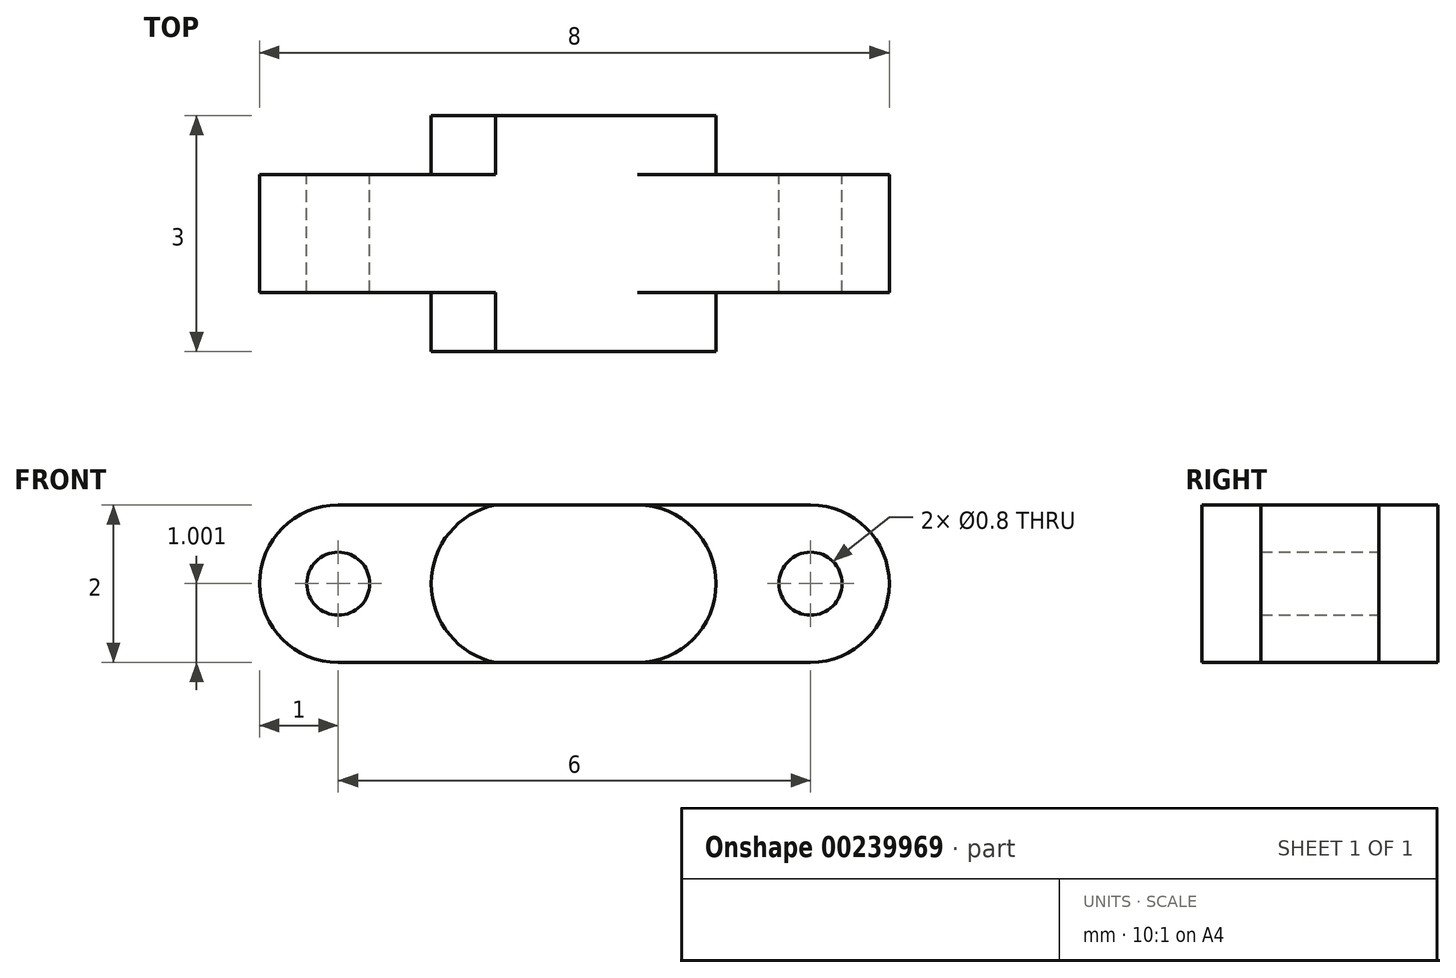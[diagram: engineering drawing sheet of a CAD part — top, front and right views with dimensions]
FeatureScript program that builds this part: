
annotation { "Feature Type Name" : "Feature", "Feature Type Description" : "" }
export const myFeature = defineFeature(function(context is Context, id is Id, definition is map)
    precondition{}
    {
        {
            var Q0;
            Q0=qCreatedBy(makeId("Front.planeOp"),FACE);
            var sketch = newSketch(context, id + "F0", { "sketchPlane" : qUnion([Q0])});
            skLineSegment(sketch, "E0.bottom", {"start": v(-1, -0.25) * mm, "end": v(-6, -0.25) * mm});
            skLineSegment(sketch, "E0.top", {"start": v(-1, -2.25) * mm, "end": v(-6, -2.25) * mm});
            skArc(sketch, "E1", {"start": v(0, -2.25) * mm, "mid": v(1, -1.25) * mm, "end": v(0, -0.25) * mm});
            skLineSegment(sketch, "E2", {"start": v(-1, -0.25) * mm, "end": v(0, -0.25) * mm});
            skLineSegment(sketch, "E3", {"start": v(-1, -2.25) * mm, "end": v(0, -2.25) * mm});
            skArc(sketch, "E4", {"start": v(-4, -0.25) * mm, "mid": v(-4.82, -1.25) * mm, "end": v(-4, -2.25) * mm});
            skPoint(sketch, "E5", {"position": v(-6, -1.25) * mm});
            skCircle(sketch, "E6", {"center": v(-6, -1.25) * mm, "radius": 0.4 * mm});
            skCircle(sketch, "E7", {"center": v(0, -1.25) * mm, "radius": 0.4 * mm});
            skArc(sketch, "E8", {"start": v(-2.2, -2.25) * mm, "mid": v(-1.2, -1.25) * mm, "end": v(-2.2, -0.25) * mm});
            skLineSegment(sketch, "E9", {"start": v(-6, -0.25) * mm, "end": v(-6, -0.25) * mm});
            skArc(sketch, "E10", {"start": v(-6, -0.25) * mm, "mid": v(-7, -1.25) * mm, "end": v(-6, -2.25) * mm});
            skLineSegment(sketch, "E11", {"start": v(-7, -1.25) * mm, "end": v(1, -1.25) * mm, "construction": true});
            skSolve(sketch);
        }
        {
            var Q0;
            {var subQ5=sQuery(id+"F0.wireOp",EDGE,"E4");Q0=makeQuery(id+"F0.imprint","IMPRINT",FACE,{"disambiguationData":[TD([[makeQuery(id+"F0.imprint","IMPRINT",EDGE,{"derivedFrom":subQ5}),1.0]])]});}
            var Q1;
            Q1=makeQuery(id+"F0.imprint","IMPRINT",FACE,{"disambiguationData":[TD([[makeQuery(id+"F0.imprint","IMPRINT",EDGE,{"derivedFrom":sQuery(id+"F0.wireOp",EDGE,"E1")}),1.0]])]});
            var Q2;
            {var subQ0=sQuery(id+"F0.wireOp",EDGE,"bQbziyav-jX1J-XLfE-gFu1-S9SHtQTFnJFi");var subQ1=sQuery(id+"F0.wireOp",EDGE,"Mre1yFln-Q6Go-vBB8-nmWn-4SXoC3vIunpy");var subQ2=makeQuery(id+"F0.imprint","INTERSECT",VERTEX,{"derivedFrom":[subQ1,subQ0]});Q2=makeQuery(id+"F0.imprint","IMPRINT",FACE,{"disambiguationData":[TD([[makeQuery(id+"F0.imprint","IMPRINT",EDGE,{"disambiguationData":[TD([[subQ2,1.0]])],"derivedFrom":subQ1}),1.0]])]});}
            var Q3;
            {var subQ1=sQuery(id+"F0.wireOp",EDGE,"E0.bottom");var subQ3=sQuery(id+"F0.wireOp",EDGE,"Mre1yFln-Q6Go-vBB8-nmWn-4SXoC3vIunpy");var subQ4=makeQuery(id+"F0.imprint","INTERSECT",VERTEX,{"derivedFrom":[subQ1,subQ3]});Q3=makeQuery(id+"F0.imprint","IMPRINT",FACE,{"disambiguationData":[TD([[makeQuery(id+"F0.imprint","IMPRINT",EDGE,{"disambiguationData":[TD([[subQ4,-1.0]])],"derivedFrom":subQ3}),1.0]])]});}
            var Q4;
            {var subQ1=sQuery(id+"F0.wireOp",EDGE,"E0.top");var subQ3=sQuery(id+"F0.wireOp",EDGE,"bQbziyav-jX1J-XLfE-gFu1-S9SHtQTFnJFi");var subQ4=makeQuery(id+"F0.imprint","INTERSECT",VERTEX,{"derivedFrom":[subQ1,subQ3]});Q4=makeQuery(id+"F0.imprint","IMPRINT",FACE,{"disambiguationData":[TD([[makeQuery(id+"F0.imprint","IMPRINT",EDGE,{"disambiguationData":[TD([[subQ4,1.0]])],"derivedFrom":subQ3}),1.0]])]});}
            var Q5;
            {var subQ0=sQuery(id+"F0.wireOp",EDGE,"E4");Q5=makeQuery(id+"F0.imprint","IMPRINT",FACE,{"disambiguationData":[TD([[makeQuery(id+"F0.imprint","IMPRINT",EDGE,{"derivedFrom":subQ0}),-1.0]])]});}
            var Q6;
            {var subQ1=sQuery(id+"F0.wireOp",EDGE,"E0.bottom");var subQ3=sQuery(id+"F0.wireOp",EDGE,"E8");var subQ4=makeQuery(id+"F0.imprint","INTERSECT",VERTEX,{"derivedFrom":[subQ1,subQ3]});Q6=makeQuery(id+"F0.imprint","IMPRINT",FACE,{"disambiguationData":[TD([[makeQuery(id+"F0.imprint","IMPRINT",EDGE,{"disambiguationData":[TD([[subQ4,1.0]])],"derivedFrom":subQ3}),-1.0]])]});}
            var Q7;
            {var subQ1=sQuery(id+"F0.wireOp",EDGE,"E0.top");var subQ3=sQuery(id+"F0.wireOp",EDGE,"E8");var subQ4=makeQuery(id+"F0.imprint","INTERSECT",VERTEX,{"derivedFrom":[subQ1,subQ3]});Q7=makeQuery(id+"F0.imprint","IMPRINT",FACE,{"disambiguationData":[TD([[makeQuery(id+"F0.imprint","IMPRINT",EDGE,{"disambiguationData":[TD([[subQ4,-1.0]])],"derivedFrom":subQ3}),-1.0]])]});}
            extrude(context, id + "F1", {"entities" : qUnion([Q0, Q1, Q2, Q3, Q4, Q5, Q6, Q7]), "depth" : 1.5 * mm});
        }
        {
            var Q0;
            {var subQ0=sQuery(id+"F0.wireOp",EDGE,"E4");Q0=makeQuery(id+"F0.imprint","IMPRINT",FACE,{"disambiguationData":[TD([[makeQuery(id+"F0.imprint","IMPRINT",EDGE,{"derivedFrom":subQ0}),1.0]])]});}
            var Q1;
            {var subQ0=sQuery(id+"F0.wireOp",EDGE,"bQbziyav-jX1J-XLfE-gFu1-S9SHtQTFnJFi");var subQ1=sQuery(id+"F0.wireOp",EDGE,"Mre1yFln-Q6Go-vBB8-nmWn-4SXoC3vIunpy");var subQ2=makeQuery(id+"F0.imprint","INTERSECT",VERTEX,{"derivedFrom":[subQ1,subQ0]});Q1=makeQuery(id+"F0.imprint","IMPRINT",FACE,{"disambiguationData":[TD([[makeQuery(id+"F0.imprint","IMPRINT",EDGE,{"disambiguationData":[TD([[subQ2,1.0]])],"derivedFrom":subQ1}),1.0]])]});}
            extrude(context, id + "F2", {"entities" : qUnion([Q0, Q1]), "operationType" : NewBodyOperationType.ADD, "oppositeDirection" : true, "depth" : 0.75 * mm, "hasSecondDirection" : true, "secondDirectionOppositeDirection" : false, "secondDirectionDepth" : 2.25 * mm});
        }
    });
